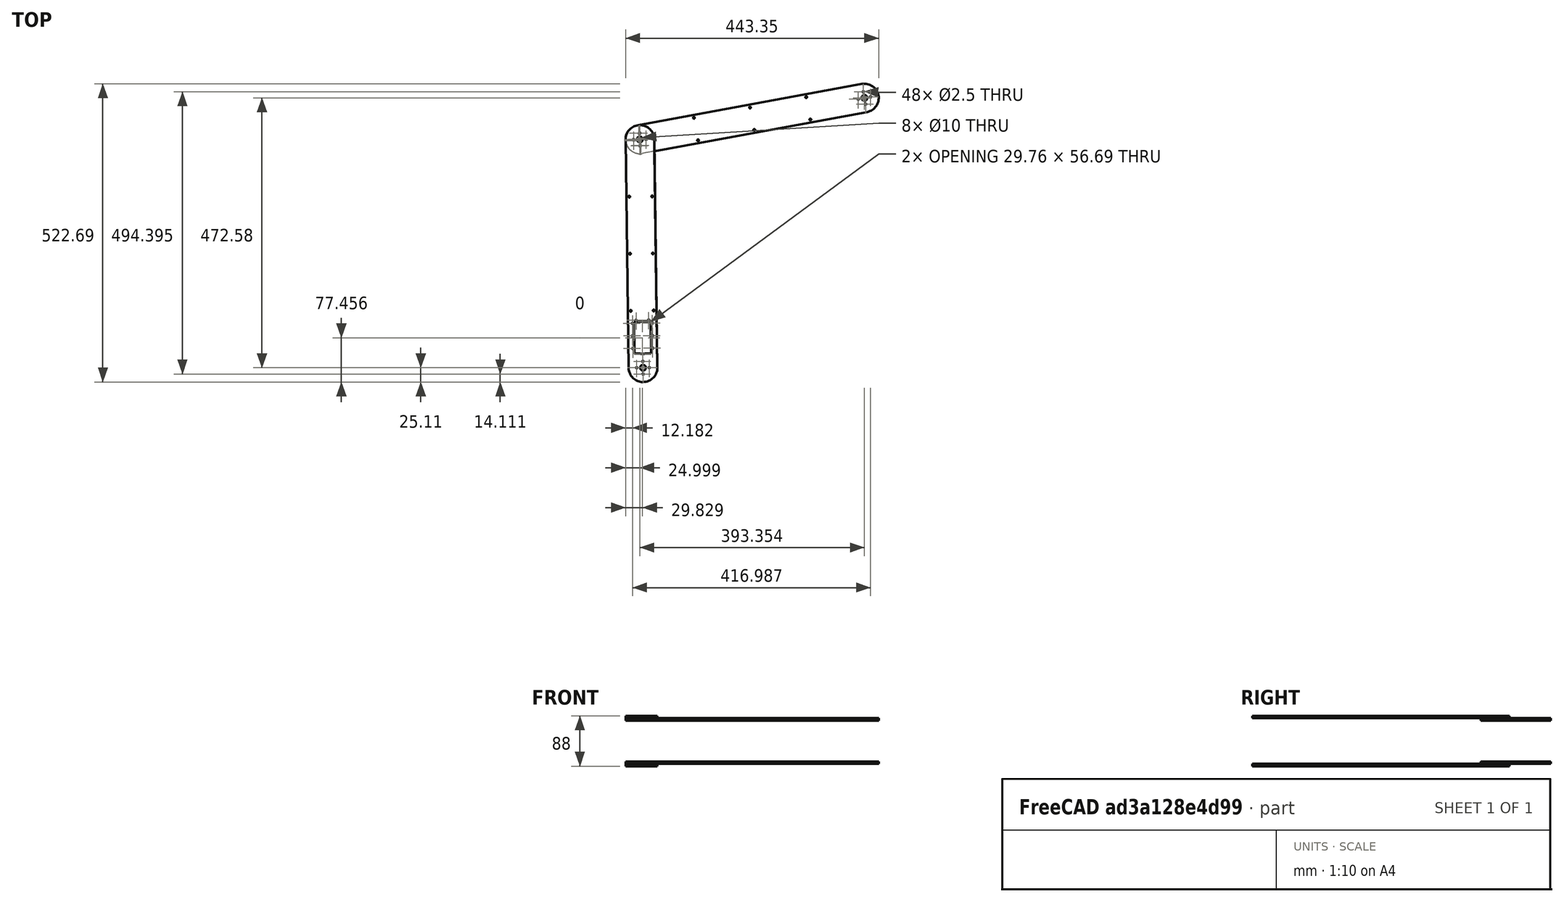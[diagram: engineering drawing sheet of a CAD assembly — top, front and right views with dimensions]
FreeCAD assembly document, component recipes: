
FREECAD ASSEMBLY — COMPONENT RECIPES ("arm_assembly4")

This assembly document has 12 components, labeled P0..P11 below (a component is one placed body or linked part). 8 of them carry a construction recipe — the FreeCAD feature program that regenerates the part from scratch, quoted from this document or its linked companion documents; the rest are supplied as boundary geometry only. No exploded tour is included for this assembly.
COMPONENT P0 — recipe-attached ("arm_low_1", modeled in this document).
Construction recipe (the document's own serialized feature program — sketch geometry with constraints, then the solid features built on it; lengths are millimeters unless a unit is written):

FEATURE [Sketcher::SketchObject] Sketch
  ArcFitTolerance = 1e-06
  AttachmentSupport = -> [XY_Plane]
  FullyConstrained = false
  MakeInternals = false
  MapMode = 5
  sketch-geometry (67):
    g0: LineSegment [constr] StartX=1.5008e-12 StartY=20 StartZ=0 EndX=1.5008e-12 EndY=-20 EndZ=0
    g1: LineSegment [constr] StartX=-2.359e-12 StartY=0 StartZ=0 EndX=-2.359e-12 EndY=400 EndZ=0
    g2: LineSegment [constr] StartX=1.5008e-12 StartY=20 StartZ=0 EndX=1.5008e-12 EndY=25 EndZ=0
    g3: Circle CenterX=-2.359e-12 CenterY=400 CenterZ=0 NormalX=0 NormalY=0 NormalZ=1 AngleXU=0 Radius=5
    g4: Circle CenterX=-2.359e-12 CenterY=400 CenterZ=0 NormalX=0 NormalY=0 NormalZ=1 AngleXU=0 Radius=2
    g5: Circle CenterX=-10.9997 CenterY=400 CenterZ=0 NormalX=0 NormalY=0 NormalZ=1 AngleXU=0 Radius=1.25
    g6: Circle CenterX=0 CenterY=389 CenterZ=0 NormalX=0 NormalY=0 NormalZ=1 AngleXU=0 Radius=1.25
    g7: Circle CenterX=10.9997 CenterY=400 CenterZ=0 NormalX=0 NormalY=0 NormalZ=1 AngleXU=0 Radius=1.25
    g8: Circle CenterX=0 CenterY=411 CenterZ=0 NormalX=0 NormalY=0 NormalZ=1 AngleXU=0 Radius=1.25
    g9: LineSegment [constr] StartX=0 StartY=-5 StartZ=0 EndX=0 EndY=5.99996 EndZ=0
    g10: Circle [constr] CenterX=0 CenterY=0 CenterZ=0 NormalX=0 NormalY=0 NormalZ=1 AngleXU=0 Radius=14
    g11: LineSegment [constr] StartX=0 StartY=0 StartZ=0 EndX=25.23 EndY=0 EndZ=0
    g12: Circle [constr] CenterX=0 CenterY=-3.8e-05 CenterZ=0 NormalX=0 NormalY=0 NormalZ=1 AngleXU=0 Radius=11
    g13: Circle CenterX=0 CenterY=0 CenterZ=0 NormalX=0 NormalY=0 NormalZ=1 AngleXU=0 Radius=5
    g14: Circle CenterX=10.9997 CenterY=0 CenterZ=0 NormalX=0 NormalY=0 NormalZ=1 AngleXU=0 Radius=1.25
    g15: Circle CenterX=-10.9997 CenterY=0 CenterZ=0 NormalX=0 NormalY=0 NormalZ=1 AngleXU=0 Radius=1.25
    g16: Circle CenterX=0 CenterY=-10.9997 CenterZ=0 NormalX=0 NormalY=0 NormalZ=1 AngleXU=0 Radius=1.25
    g17: Circle CenterX=0 CenterY=11 CenterZ=0 NormalX=0 NormalY=0 NormalZ=1 AngleXU=0 Radius=1.25
    g18: LineSegment [constr] StartX=0 StartY=0 StartZ=0 EndX=-25 EndY=0 EndZ=0
    g19: LineSegment [constr] StartX=20.1368 StartY=86.0999 StartZ=0 EndX=20.1368 EndY=24.9999 EndZ=0
    g20: LineSegment [constr] StartX=0.036848 StartY=80.5 StartZ=0 EndX=14.5368 EndY=80.5 EndZ=0
    g21: LineSegment StartX=14.5368 StartY=80.5 StartZ=0 EndX=-14.4632 EndY=80.5 EndZ=0
    g22: LineSegment StartX=14.5368 StartY=80.5 StartZ=0 EndX=14.5368 EndY=24.9999 EndZ=0
    g23: Circle CenterX=11.0368 CenterY=83.3 CenterZ=0 NormalX=0 NormalY=0 NormalZ=1 AngleXU=0 Radius=1.25
    g24: Circle CenterX=17.3368 CenterY=78 CenterZ=0 NormalX=0 NormalY=0 NormalZ=1 AngleXU=0 Radius=1.25
    g25: LineSegment [constr] StartX=-20.0632 StartY=86.0999 StartZ=0 EndX=20.1368 EndY=86.0999 EndZ=0
    g26: Circle CenterX=17.3368 CenterY=56 CenterZ=0 NormalX=0 NormalY=0 NormalZ=1 AngleXU=0 Radius=1.25
    g27: Circle CenterX=17.3368 CenterY=34 CenterZ=0 NormalX=0 NormalY=0 NormalZ=1 AngleXU=0 Radius=1.25
    g28: Circle [constr] CenterX=0.036848 CenterY=37.9999 CenterZ=0 NormalX=0 NormalY=0 NormalZ=1 AngleXU=0 Radius=14
    g29: ArcOfCircle CenterX=0.036848 CenterY=37.9999 CenterZ=0 NormalX=0 NormalY=0 NormalZ=1 AngleXU=0 Radius=14 StartAngle=4.33214 EndAngle=5.09264
    g30: LineSegment StartX=5.233 StartY=24.9999 StartZ=0 EndX=14.5368 EndY=24.9999 EndZ=0
    g31: LineSegment [constr] StartX=14.5368 StartY=24.9999 StartZ=0 EndX=20.1368 EndY=24.9999 EndZ=0
    g32: LineSegment [constr] StartX=17.3368 StartY=56 StartZ=0 EndX=-17.2632 EndY=56 EndZ=0
    g33: LineSegment [constr] StartX=-20.0632 StartY=24.9999 StartZ=0 EndX=-20.0632 EndY=86.0999 EndZ=0
    g34: LineSegment StartX=-14.4632 StartY=80.5 StartZ=0 EndX=-14.4632 EndY=24.9999 EndZ=0
    g35: Circle CenterX=-17.2632 CenterY=78 CenterZ=0 NormalX=0 NormalY=0 NormalZ=1 AngleXU=0 Radius=1.25
    g36: Circle CenterX=-10.9632 CenterY=83.3 CenterZ=0 NormalX=0 NormalY=0 NormalZ=1 AngleXU=0 Radius=1.25
    g37: Circle CenterX=-17.2632 CenterY=56 CenterZ=0 NormalX=0 NormalY=0 NormalZ=1 AngleXU=0 Radius=1.25
    g38: Circle CenterX=-17.2632 CenterY=34 CenterZ=0 NormalX=0 NormalY=0 NormalZ=1 AngleXU=0 Radius=1.25
    g39: LineSegment StartX=-14.4632 StartY=24.9999 StartZ=0 EndX=-5.15931 EndY=24.9999 EndZ=0
    g40: LineSegment [constr] StartX=-20.0632 StartY=24.9999 StartZ=0 EndX=-14.4632 EndY=24.9999 EndZ=0
    g41: ArcOfCircle CenterX=0.115002 CenterY=3.75548e-06 CenterZ=0 NormalX=0 NormalY=0 NormalZ=1 AngleXU=0 Radius=25.115 StartAngle=3.14159 EndAngle=6.28319
    g42: ArcOfCircle CenterX=0.115002 CenterY=399.959 CenterZ=0 NormalX=0 NormalY=0 NormalZ=1 AngleXU=0 Radius=25.115 StartAngle=0 EndAngle=3.14159
    g43: LineSegment StartX=-25 StartY=3.75548e-06 StartZ=0 EndX=-25 EndY=399.959 EndZ=0
    g44: LineSegment StartX=25.23 StartY=3.75548e-06 StartZ=0 EndX=25.23 EndY=399.959 EndZ=0
    g45: LineSegment [constr] StartX=25.23 StartY=199.98 StartZ=0 EndX=-25 EndY=199.98 EndZ=0
    g46: LineSegment [constr] StartX=25.23 StartY=199.98 StartZ=0 EndX=55.23 EndY=199.98 EndZ=0
    g47: LineSegment [constr] StartX=25.23 StartY=0 StartZ=0 EndX=55.23 EndY=0 EndZ=0
    g48: LineSegment [constr] StartX=55.23 StartY=0 StartZ=0 EndX=55.23 EndY=199.98 EndZ=0
    g49: LineSegment [constr] StartX=55.23 StartY=99.9898 StartZ=0 EndX=25.23 EndY=99.9898 EndZ=0
    g50: LineSegment [constr] StartX=25.23 StartY=99.9898 StartZ=0 EndX=-25 EndY=99.9898 EndZ=0
    g51: LineSegment [constr] StartX=25.23 StartY=399.959 StartZ=0 EndX=55.23 EndY=399.959 EndZ=0
    g52: LineSegment [constr] StartX=55.23 StartY=399.959 StartZ=0 EndX=55.23 EndY=199.98 EndZ=0
    g53: LineSegment [constr] StartX=55.23 StartY=299.969 StartZ=0 EndX=25.23 EndY=299.969 EndZ=0
    g54: LineSegment [constr] StartX=25.23 StartY=299.969 StartZ=0 EndX=-25 EndY=299.969 EndZ=0
    g55: LineSegment [constr] StartX=-25 StartY=299.969 StartZ=0 EndX=-20 EndY=299.969 EndZ=0
    g56: LineSegment [constr] StartX=-20 StartY=299.969 StartZ=0 EndX=-20 EndY=199.98 EndZ=0
    g57: LineSegment [constr] StartX=-20 StartY=199.98 StartZ=0 EndX=-20 EndY=99.9898 EndZ=0
    g58: LineSegment [constr] StartX=25.23 StartY=299.969 StartZ=0 EndX=20.23 EndY=299.969 EndZ=0
    g59: LineSegment [constr] StartX=20.23 StartY=299.969 StartZ=0 EndX=20.23 EndY=199.98 EndZ=0
    g60: LineSegment [constr] StartX=20.23 StartY=199.98 StartZ=0 EndX=20.23 EndY=99.9898 EndZ=0
    g61: Circle CenterX=-20 CenterY=299.969 CenterZ=0 NormalX=0 NormalY=0 NormalZ=1 AngleXU=0 Radius=1.5
    g62: Circle CenterX=20.23 CenterY=299.969 CenterZ=0 NormalX=0 NormalY=0 NormalZ=1 AngleXU=0 Radius=1.5
    g63: Circle CenterX=-20 CenterY=199.98 CenterZ=0 NormalX=0 NormalY=0 NormalZ=1 AngleXU=0 Radius=1.5
    g64: Circle CenterX=20.23 CenterY=199.98 CenterZ=0 NormalX=0 NormalY=0 NormalZ=1 AngleXU=0 Radius=1.5
    g65: Circle CenterX=-20 CenterY=99.9898 CenterZ=0 NormalX=0 NormalY=0 NormalZ=1 AngleXU=0 Radius=1.5
    g66: Circle CenterX=20.23 CenterY=99.9898 CenterZ=0 NormalX=0 NormalY=0 NormalZ=1 AngleXU=0 Radius=1.5
  constraints (132):
    c: Vertical(g0)
    c: Vertical(g1)
    c: Coincident(g2,g0)
    c: Vertical(g2)
    c: Diameter(g3) = 10
    c: Coincident(g3,g1)
    c: Diameter(g4) = 4
    c: Coincident(g4,g1)
    c: Diameter(g8) = 2.5
    c: Diameter(g5) = 2.5
    c: Diameter(g6) = 2.5
    c: Diameter(g7) = 2.5
    c: Vertical(g9)
    c: Diameter(g10) = 28
    c: Coincident(g18,g10)
    c: Horizontal(g18)
    c: Coincident(g11,g10)
    c: Horizontal(g11)
    c: Diameter(g12) = 22
    c: Diameter(g13) = 10
    c: Coincident(g13,g10)
    c: Diameter(g17) = 2.5
    c: Diameter(g15) = 2.5
    c: Diameter(g16) = 2.5
    c: Diameter(g14) = 2.5
    c: Coincident(g25,g19)
    c: Coincident(g33,g25)
    c: Horizontal(g25)
    c: Vertical(g19)
    c: Vertical(g33)
    c: Distance(g19,g33) = 40.2
    c: Distance(g25,g33) = 61.1
    c: Diameter(g29) = 28
    c: Horizontal(g20)
    c: Coincident(g21,g20)
    c: Horizontal(g21)
    c: Coincident(g34,g21)
    c: Vertical(g34)
    c: Coincident(g22,g20)
    c: Vertical(g22)
    c: Diameter(g23) = 2.5
    c: Equal(g23,g36)
    c: Equal(g23,g27)
    c: Equal(g23,g38)
    c: Equal(g23,g37)
    c: Equal(g23,g35)
    c: Equal(g23,g24)
    c: Equal(g23,g26)
    c: Coincident(g28,g29)
    c: PointOnObject(g29,g28)
    c: Coincident(g30,g29)
    c: Coincident(g30,g22)
    c: Horizontal(g30)
    c: Coincident(g31,g22)
    c: Coincident(g31,g19)
    c: Horizontal(g31)
    c: Coincident(g39,g34)
    c: Coincident(g39,g29)
    c: Horizontal(g39)
    c: Coincident(g40,g33)
    c: Coincident(g40,g34)
    c: Horizontal(g40)
    c: Coincident(g32,g26)
    c: Coincident(g32,g37)
    c: Horizontal(g32)
    c: DistanceY(g28,g1) = 362
    c: Tangent(g41,g43) = 1.5708
    c: Tangent(g41,g44) = -1.5708
    c: Tangent(g42,g43) = 1.5708
    c: Tangent(g42,g44) = -1.5708
    c: Equal(g41,g42)
    c: Symmetric(g44,g44,g45)
    c: Symmetric(g43,g43,g45)
    c: Horizontal(g45)
    c: Distance(g46) = 30
    c: Horizontal(g46)
    c: Coincident(g46,g45)
    c: Distance(g47) = 30
    c: Horizontal(g47)
    c: Coincident(g47,g11)
    c: PointOnObject(g47,g-1)
    c: Coincident(g48,g47)
    c: Coincident(g48,g46)
    c: Vertical(g48)
    c: Symmetric(g48,g48,g49)
    c: PointOnObject(g49,g44)
    c: Horizontal(g49)
    c: Coincident(g50,g49)
    c: PointOnObject(g50,g43)
    c: Horizontal(g50)
    c: Distance(g51) = 30
    c: Horizontal(g51)
    c: Coincident(g51,g42)
    c: Coincident(g52,g51)
    c: Coincident(g52,g46)
    c: Symmetric(g52,g52,g53)
    c: PointOnObject(g53,g44)
    c: Horizontal(g53)
    c: Coincident(g54,g53)
    c: PointOnObject(g54,g43)
    c: Horizontal(g54)
    c: Distance(g55) = 5
    c: Coincident(g55,g54)
    c: PointOnObject(g55,g54)
    c: Coincident(g56,g55)
    c: PointOnObject(g56,g45)
    c: Vertical(g56)
    c: Coincident(g57,g56)
    c: PointOnObject(g57,g50)
    c: Vertical(g57)
    c: Distance(g58) = 5
    c: Coincident(g58,g53)
    c: PointOnObject(g58,g54)
    c: Coincident(g59,g58)
    c: PointOnObject(g59,g45)
    c: Vertical(g59)
    c: Coincident(g60,g59)
    c: PointOnObject(g60,g50)
    c: Vertical(g60)
    c: Coincident(g61,g55)
    c: Diameter(g61) = 3
    c: Coincident(g62,g58)
    c: Equal(g61,g62)
    c: Coincident(g63,g56)
    c: Equal(g61,g63)
    c: Coincident(g64,g59)
    c: Equal(g63,g64)
    c: Coincident(g65,g57)
    c: Equal(g63,g65)
    c: Coincident(g66,g60)
    c: Equal(g65,g66)
    c: DistanceY(g41,g28) = 37.9999
FEATURE [PartDesign::Pad] Pad
  Direction = (0,0,1)
  Length = 4
  Length2 = 10
  Profile = -> Sketch
  ReferenceAxis = -> Sketch [N_Axis]
  Refine = true
  Suppressed = false
  Type = 0
FEATURE [PartDesign::Body] Body  label="arm_low_1"
  AllowCompound = false
  Group = -> [Sketch,Pad]
  Origin = -> Origin
  Placement = pos=(0,0,25.3) rot=(0,0,1;0.013804rad)
  Tip = -> Pad
COMPONENT P1 — recipe-attached ("arm_high_1", modeled in this document).
Construction recipe (the document's own serialized feature program — sketch geometry with constraints, then the solid features built on it; lengths are millimeters unless a unit is written):

FEATURE [Sketcher::SketchObject] Sketch001
  ArcFitTolerance = 1e-06
  FullyConstrained = false
  MakeInternals = false
  MapMode = 5
  sketch-geometry (41):
    g0: Circle [constr] CenterX=7e-16 CenterY=0.000303 CenterZ=0 NormalX=0 NormalY=0 NormalZ=1 AngleXU=0 Radius=14
    g1: LineSegment [constr] StartX=7e-16 StartY=0.000303 StartZ=0 EndX=7e-16 EndY=400.001 EndZ=0
    g2: Circle CenterX=7e-16 CenterY=400.001 CenterZ=0 NormalX=0 NormalY=0 NormalZ=1 AngleXU=0 Radius=5
    g3: Circle CenterX=7e-16 CenterY=0 CenterZ=0 NormalX=0 NormalY=0 NormalZ=1 AngleXU=0 Radius=5
    g4: Circle CenterX=7e-16 CenterY=400.001 CenterZ=0 NormalX=0 NormalY=0 NormalZ=1 AngleXU=0 Radius=2
    g5: Circle CenterX=7e-16 CenterY=0.000303 CenterZ=0 NormalX=0 NormalY=0 NormalZ=1 AngleXU=0 Radius=2
    g6: Circle [constr] CenterX=0 CenterY=0 CenterZ=0 NormalX=0 NormalY=0 NormalZ=1 AngleXU=0 Radius=11
    g7: ArcOfCircle CenterX=7e-16 CenterY=0 CenterZ=0 NormalX=0 NormalY=0 NormalZ=1 AngleXU=0 Radius=25 StartAngle=3.14159 EndAngle=6.28319
    g8: ArcOfCircle CenterX=7e-16 CenterY=400.001 CenterZ=0 NormalX=0 NormalY=0 NormalZ=1 AngleXU=0 Radius=25 StartAngle=6e-16 EndAngle=3.14159
    g9: LineSegment StartX=-25 StartY=-8e-15 StartZ=0 EndX=-25 EndY=400.001 EndZ=0
    g10: LineSegment StartX=25 StartY=0 StartZ=0 EndX=25 EndY=400.001 EndZ=0
    g11: Circle CenterX=10.9997 CenterY=400.001 CenterZ=0 NormalX=0 NormalY=0 NormalZ=1 AngleXU=0 Radius=1.25
    g12: Circle CenterX=0 CenterY=411.001 CenterZ=0 NormalX=0 NormalY=0 NormalZ=1 AngleXU=0 Radius=1.25
    g13: Circle CenterX=-10.9997 CenterY=400.001 CenterZ=0 NormalX=0 NormalY=0 NormalZ=1 AngleXU=0 Radius=1.25
    g14: Circle CenterX=0 CenterY=389.001 CenterZ=0 NormalX=0 NormalY=0 NormalZ=1 AngleXU=0 Radius=1.25
    g15: Circle CenterX=10.9997 CenterY=0.000303 CenterZ=0 NormalX=0 NormalY=0 NormalZ=1 AngleXU=0 Radius=1.25
    g16: Circle CenterX=0 CenterY=11 CenterZ=0 NormalX=0 NormalY=0 NormalZ=1 AngleXU=0 Radius=1.25
    g17: Circle CenterX=-10.9997 CenterY=0.000303 CenterZ=0 NormalX=0 NormalY=0 NormalZ=1 AngleXU=0 Radius=1.25
    g18: Circle CenterX=0 CenterY=-10.9994 CenterZ=0 NormalX=0 NormalY=0 NormalZ=1 AngleXU=0 Radius=1.25
    g19: LineSegment [constr] StartX=25 StartY=200 StartZ=0 EndX=-25 EndY=200 EndZ=0
    g20: LineSegment [constr] StartX=25 StartY=200 StartZ=0 EndX=55 EndY=200 EndZ=0
    g21: LineSegment [constr] StartX=25 StartY=0 StartZ=0 EndX=55 EndY=0 EndZ=0
    g22: LineSegment [constr] StartX=25 StartY=400.001 StartZ=0 EndX=55 EndY=400.001 EndZ=0
    g23: LineSegment [constr] StartX=55 StartY=200 StartZ=0 EndX=55 EndY=400.001 EndZ=0
    g24: LineSegment [constr] StartX=55 StartY=200 StartZ=0 EndX=55 EndY=0 EndZ=0
    g25: LineSegment [constr] StartX=55 StartY=100 StartZ=0 EndX=25 EndY=100 EndZ=0
    g26: LineSegment [constr] StartX=25 StartY=100 StartZ=0 EndX=-25 EndY=100 EndZ=0
    g27: LineSegment [constr] StartX=55 StartY=300 StartZ=0 EndX=25 EndY=300 EndZ=0
    g28: LineSegment [constr] StartX=25 StartY=300 StartZ=0 EndX=-25 EndY=300 EndZ=0
    g29: LineSegment [constr] StartX=-25 StartY=300 StartZ=0 EndX=-20 EndY=300 EndZ=0
    g30: LineSegment [constr] StartX=-20 StartY=300 StartZ=0 EndX=-20 EndY=200 EndZ=0
    g31: LineSegment [constr] StartX=-20 StartY=200 StartZ=0 EndX=-20 EndY=100 EndZ=0
    g32: LineSegment [constr] StartX=25 StartY=100 StartZ=0 EndX=20 EndY=100 EndZ=0
    g33: LineSegment [constr] StartX=20 StartY=100 StartZ=0 EndX=20 EndY=200 EndZ=0
    g34: LineSegment [constr] StartX=20 StartY=200 StartZ=0 EndX=20 EndY=300 EndZ=0
    g35: Circle CenterX=-20 CenterY=300 CenterZ=0 NormalX=0 NormalY=0 NormalZ=1 AngleXU=0 Radius=1.5
    g36: Circle CenterX=20 CenterY=300 CenterZ=0 NormalX=0 NormalY=0 NormalZ=1 AngleXU=0 Radius=1.5
    g37: Circle CenterX=-20 CenterY=200 CenterZ=0 NormalX=0 NormalY=0 NormalZ=1 AngleXU=0 Radius=1.5
    g38: Circle CenterX=20 CenterY=200 CenterZ=0 NormalX=0 NormalY=0 NormalZ=1 AngleXU=0 Radius=1.5
    g39: Circle CenterX=-20 CenterY=100 CenterZ=0 NormalX=0 NormalY=0 NormalZ=1 AngleXU=0 Radius=1.5
    g40: Circle CenterX=20 CenterY=100 CenterZ=0 NormalX=0 NormalY=0 NormalZ=1 AngleXU=0 Radius=1.5
  constraints (85):
    c: Diameter(g0) = 28
    c: Coincident(g1,g0)
    c: Vertical(g1)
    c: Coincident(g2,g1)
    c: Diameter(g3) = 10
    c: Diameter(g4) = 4
    c: Coincident(g4,g1)
    c: Diameter(g5) = 4
    c: Coincident(g5,g0)
    c: Diameter(g6) = 22
    c: Tangent(g7,g9) = 1.5708
    c: Tangent(g7,g10) = -1.5708
    c: Tangent(g8,g9) = 1.5708
    c: Tangent(g8,g10) = -1.5708
    c: Equal(g7,g8)
    c: Radius(g7) = 25
    c: Coincident(g7,g3)
    c: Coincident(g8,g1)
    c: Vertical(g9)
    c: Diameter(g12) = 2.5
    c: Diameter(g13) = 2.5
    c: Diameter(g14) = 2.5
    c: Diameter(g11) = 2.5
    c: Diameter(g16) = 2.5
    c: Diameter(g17) = 2.5
    c: Diameter(g18) = 2.5
    c: Diameter(g15) = 2.5
    c: Symmetric(g10,g10,g19)
    c: Symmetric(g9,g9,g19)
    c: Distance(g20) = 30
    c: Horizontal(g20)
    c: Coincident(g20,g19)
    c: Distance(g21) = 30
    c: Horizontal(g21)
    c: Coincident(g21,g7)
    c: PointOnObject(g21,g-1)
    c: Distance(g22) = 30
    c: Horizontal(g22)
    c: Coincident(g22,g8)
    c: Coincident(g23,g20)
    c: Coincident(g23,g22)
    c: Coincident(g24,g20)
    c: Coincident(g24,g21)
    c: Symmetric(g24,g24,g25)
    c: PointOnObject(g25,g10)
    c: Horizontal(g25)
    c: Coincident(g26,g25)
    c: PointOnObject(g26,g9)
    c: Horizontal(g26)
    c: Symmetric(g23,g23,g27)
    c: PointOnObject(g27,g10)
    c: Horizontal(g27)
    c: Coincident(g28,g27)
    c: PointOnObject(g28,g9)
    c: Horizontal(g28)
    c: Distance(g29) = 5
    c: Horizontal(g29)
    c: Coincident(g29,g28)
    c: Coincident(g30,g29)
    c: PointOnObject(g30,g19)
    c: Vertical(g30)
    c: Coincident(g31,g30)
    c: PointOnObject(g31,g26)
    c: Vertical(g31)
    c: Distance(g32) = 5
    c: Horizontal(g32)
    c: Coincident(g32,g25)
    c: Coincident(g33,g32)
    c: PointOnObject(g33,g19)
    c: Vertical(g33)
    c: Coincident(g34,g33)
    c: PointOnObject(g34,g28)
    c: Vertical(g34)
    c: Diameter(g35) = 3
    c: Coincident(g35,g29)
    c: Coincident(g36,g34)
    c: Equal(g35,g36)
    c: Coincident(g37,g30)
    c: Equal(g35,g37)
    c: Coincident(g38,g33)
    c: Equal(g37,g38)
    c: Coincident(g39,g31)
    c: Equal(g37,g39)
    c: Coincident(g40,g32)
    c: Equal(g39,g40)
FEATURE [PartDesign::Pad] Pad001
  Direction = (0,0,1)
  Length = 4
  Length2 = 10
  Profile = -> Sketch001
  ReferenceAxis = -> Sketch001 [N_Axis]
  Refine = true
  Suppressed = false
  Type = 0
FEATURE [PartDesign::Body] Body001  label="arm_high_1"
  AllowCompound = false
  Group = -> [Sketch001,Pad001]
  Origin = -> Origin001
  Placement = pos=(387.832,472.58,29.3) rot=(0,0,1;1.75335rad)
  Tip = -> Pad001
COMPONENT P2 — same part as P0; its construction recipe is shown at P0.
COMPONENT P3 — same part as P0; its construction recipe is shown at P0.
COMPONENT P4 — recipe-attached ("arm_low_002", modeled in this document).
Construction recipe (the document's own serialized feature program — sketch geometry with constraints, then the solid features built on it; lengths are millimeters unless a unit is written):

FEATURE [Sketcher::SketchObject] Sketch002
  ArcFitTolerance = 1e-06
  AttachmentSupport = -> [XY_Plane004]
  FullyConstrained = false
  MakeInternals = false
  MapMode = 5
  sketch-geometry (67):
    g0: LineSegment [constr] StartX=1.5008e-12 StartY=20 StartZ=0 EndX=1.5008e-12 EndY=-20 EndZ=0
    g1: LineSegment [constr] StartX=-2.359e-12 StartY=0 StartZ=0 EndX=-2.359e-12 EndY=400 EndZ=0
    g2: LineSegment [constr] StartX=1.5008e-12 StartY=20 StartZ=0 EndX=1.5008e-12 EndY=25 EndZ=0
    g3: Circle CenterX=-2.359e-12 CenterY=400 CenterZ=0 NormalX=0 NormalY=0 NormalZ=1 AngleXU=0 Radius=5
    g4: Circle CenterX=-2.359e-12 CenterY=400 CenterZ=0 NormalX=0 NormalY=0 NormalZ=1 AngleXU=0 Radius=2
    g5: Circle CenterX=-10.9997 CenterY=400 CenterZ=0 NormalX=0 NormalY=0 NormalZ=1 AngleXU=0 Radius=1.25
    g6: Circle CenterX=0 CenterY=389 CenterZ=0 NormalX=0 NormalY=0 NormalZ=1 AngleXU=0 Radius=1.25
    g7: Circle CenterX=10.9997 CenterY=400 CenterZ=0 NormalX=0 NormalY=0 NormalZ=1 AngleXU=0 Radius=1.25
    g8: Circle CenterX=0 CenterY=411 CenterZ=0 NormalX=0 NormalY=0 NormalZ=1 AngleXU=0 Radius=1.25
    g9: LineSegment [constr] StartX=0 StartY=-5 StartZ=0 EndX=0 EndY=5.99996 EndZ=0
    g10: Circle [constr] CenterX=0 CenterY=0 CenterZ=0 NormalX=0 NormalY=0 NormalZ=1 AngleXU=0 Radius=14
    g11: LineSegment [constr] StartX=0 StartY=0 StartZ=0 EndX=25.23 EndY=0 EndZ=0
    g12: Circle [constr] CenterX=0 CenterY=-3.8e-05 CenterZ=0 NormalX=0 NormalY=0 NormalZ=1 AngleXU=0 Radius=11
    g13: Circle CenterX=0 CenterY=0 CenterZ=0 NormalX=0 NormalY=0 NormalZ=1 AngleXU=0 Radius=5
    g14: Circle CenterX=10.9997 CenterY=0 CenterZ=0 NormalX=0 NormalY=0 NormalZ=1 AngleXU=0 Radius=1.25
    g15: Circle CenterX=-10.9997 CenterY=0 CenterZ=0 NormalX=0 NormalY=0 NormalZ=1 AngleXU=0 Radius=1.25
    g16: Circle CenterX=0 CenterY=-10.9997 CenterZ=0 NormalX=0 NormalY=0 NormalZ=1 AngleXU=0 Radius=1.25
    g17: Circle CenterX=0 CenterY=11 CenterZ=0 NormalX=0 NormalY=0 NormalZ=1 AngleXU=0 Radius=1.25
    g18: LineSegment [constr] StartX=0 StartY=0 StartZ=0 EndX=-25 EndY=0 EndZ=0
    g19: LineSegment [constr] StartX=20.1368 StartY=86.0999 StartZ=0 EndX=20.1368 EndY=24.9999 EndZ=0
    g20: LineSegment [constr] StartX=0.036848 StartY=80.5 StartZ=0 EndX=14.5368 EndY=80.5 EndZ=0
    g21: LineSegment StartX=14.5368 StartY=80.5 StartZ=0 EndX=-14.4632 EndY=80.5 EndZ=0
    g22: LineSegment StartX=14.5368 StartY=80.5 StartZ=0 EndX=14.5368 EndY=24.9999 EndZ=0
    g23: Circle CenterX=11.0368 CenterY=83.3 CenterZ=0 NormalX=0 NormalY=0 NormalZ=1 AngleXU=0 Radius=1.25
    g24: Circle CenterX=17.3368 CenterY=78 CenterZ=0 NormalX=0 NormalY=0 NormalZ=1 AngleXU=0 Radius=1.25
    g25: LineSegment [constr] StartX=-20.0632 StartY=86.0999 StartZ=0 EndX=20.1368 EndY=86.0999 EndZ=0
    g26: Circle CenterX=17.3368 CenterY=56 CenterZ=0 NormalX=0 NormalY=0 NormalZ=1 AngleXU=0 Radius=1.25
    g27: Circle CenterX=17.3368 CenterY=34 CenterZ=0 NormalX=0 NormalY=0 NormalZ=1 AngleXU=0 Radius=1.25
    g28: Circle [constr] CenterX=0.036848 CenterY=37.9999 CenterZ=0 NormalX=0 NormalY=0 NormalZ=1 AngleXU=0 Radius=14
    g29: ArcOfCircle CenterX=0.036848 CenterY=37.9999 CenterZ=0 NormalX=0 NormalY=0 NormalZ=1 AngleXU=0 Radius=14 StartAngle=4.33214 EndAngle=5.09264
    g30: LineSegment StartX=5.233 StartY=24.9999 StartZ=0 EndX=14.5368 EndY=24.9999 EndZ=0
    g31: LineSegment [constr] StartX=14.5368 StartY=24.9999 StartZ=0 EndX=20.1368 EndY=24.9999 EndZ=0
    g32: LineSegment [constr] StartX=17.3368 StartY=56 StartZ=0 EndX=-17.2632 EndY=56 EndZ=0
    g33: LineSegment [constr] StartX=-20.0632 StartY=24.9999 StartZ=0 EndX=-20.0632 EndY=86.0999 EndZ=0
    g34: LineSegment StartX=-14.4632 StartY=80.5 StartZ=0 EndX=-14.4632 EndY=24.9999 EndZ=0
    g35: Circle CenterX=-17.2632 CenterY=78 CenterZ=0 NormalX=0 NormalY=0 NormalZ=1 AngleXU=0 Radius=1.25
    g36: Circle CenterX=-10.9632 CenterY=83.3 CenterZ=0 NormalX=0 NormalY=0 NormalZ=1 AngleXU=0 Radius=1.25
    g37: Circle CenterX=-17.2632 CenterY=56 CenterZ=0 NormalX=0 NormalY=0 NormalZ=1 AngleXU=0 Radius=1.25
    g38: Circle CenterX=-17.2632 CenterY=34 CenterZ=0 NormalX=0 NormalY=0 NormalZ=1 AngleXU=0 Radius=1.25
    g39: LineSegment StartX=-14.4632 StartY=24.9999 StartZ=0 EndX=-5.15931 EndY=24.9999 EndZ=0
    g40: LineSegment [constr] StartX=-20.0632 StartY=24.9999 StartZ=0 EndX=-14.4632 EndY=24.9999 EndZ=0
    g41: ArcOfCircle CenterX=0.115002 CenterY=3.75548e-06 CenterZ=0 NormalX=0 NormalY=0 NormalZ=1 AngleXU=0 Radius=25.115 StartAngle=3.14159 EndAngle=6.28319
    g42: ArcOfCircle CenterX=0.115002 CenterY=399.959 CenterZ=0 NormalX=0 NormalY=0 NormalZ=1 AngleXU=0 Radius=25.115 StartAngle=0 EndAngle=3.14159
    g43: LineSegment StartX=-25 StartY=3.75548e-06 StartZ=0 EndX=-25 EndY=399.959 EndZ=0
    g44: LineSegment StartX=25.23 StartY=3.75548e-06 StartZ=0 EndX=25.23 EndY=399.959 EndZ=0
    g45: LineSegment [constr] StartX=25.23 StartY=199.98 StartZ=0 EndX=-25 EndY=199.98 EndZ=0
    g46: LineSegment [constr] StartX=25.23 StartY=199.98 StartZ=0 EndX=55.23 EndY=199.98 EndZ=0
    g47: LineSegment [constr] StartX=25.23 StartY=0 StartZ=0 EndX=55.23 EndY=0 EndZ=0
    g48: LineSegment [constr] StartX=55.23 StartY=0 StartZ=0 EndX=55.23 EndY=199.98 EndZ=0
    g49: LineSegment [constr] StartX=55.23 StartY=99.9898 StartZ=0 EndX=25.23 EndY=99.9898 EndZ=0
    g50: LineSegment [constr] StartX=25.23 StartY=99.9898 StartZ=0 EndX=-25 EndY=99.9898 EndZ=0
    g51: LineSegment [constr] StartX=25.23 StartY=399.959 StartZ=0 EndX=55.23 EndY=399.959 EndZ=0
    g52: LineSegment [constr] StartX=55.23 StartY=399.959 StartZ=0 EndX=55.23 EndY=199.98 EndZ=0
    g53: LineSegment [constr] StartX=55.23 StartY=299.969 StartZ=0 EndX=25.23 EndY=299.969 EndZ=0
    g54: LineSegment [constr] StartX=25.23 StartY=299.969 StartZ=0 EndX=-25 EndY=299.969 EndZ=0
    g55: LineSegment [constr] StartX=-25 StartY=299.969 StartZ=0 EndX=-20 EndY=299.969 EndZ=0
    g56: LineSegment [constr] StartX=-20 StartY=299.969 StartZ=0 EndX=-20 EndY=199.98 EndZ=0
    g57: LineSegment [constr] StartX=-20 StartY=199.98 StartZ=0 EndX=-20 EndY=99.9898 EndZ=0
    g58: LineSegment [constr] StartX=25.23 StartY=299.969 StartZ=0 EndX=20.23 EndY=299.969 EndZ=0
    g59: LineSegment [constr] StartX=20.23 StartY=299.969 StartZ=0 EndX=20.23 EndY=199.98 EndZ=0
    g60: LineSegment [constr] StartX=20.23 StartY=199.98 StartZ=0 EndX=20.23 EndY=99.9898 EndZ=0
    g61: Circle CenterX=-20 CenterY=299.969 CenterZ=0 NormalX=0 NormalY=0 NormalZ=1 AngleXU=0 Radius=1.5
    g62: Circle CenterX=20.23 CenterY=299.969 CenterZ=0 NormalX=0 NormalY=0 NormalZ=1 AngleXU=0 Radius=1.5
    g63: Circle CenterX=-20 CenterY=199.98 CenterZ=0 NormalX=0 NormalY=0 NormalZ=1 AngleXU=0 Radius=1.5
    g64: Circle CenterX=20.23 CenterY=199.98 CenterZ=0 NormalX=0 NormalY=0 NormalZ=1 AngleXU=0 Radius=1.5
    g65: Circle CenterX=-20 CenterY=99.9898 CenterZ=0 NormalX=0 NormalY=0 NormalZ=1 AngleXU=0 Radius=1.5
    g66: Circle CenterX=20.23 CenterY=99.9898 CenterZ=0 NormalX=0 NormalY=0 NormalZ=1 AngleXU=0 Radius=1.5
  constraints (132):
    c: Vertical(g0)
    c: Vertical(g1)
    c: Coincident(g2,g0)
    c: Vertical(g2)
    c: Diameter(g3) = 10
    c: Coincident(g3,g1)
    c: Diameter(g4) = 4
    c: Coincident(g4,g1)
    c: Diameter(g8) = 2.5
    c: Diameter(g5) = 2.5
    c: Diameter(g6) = 2.5
    c: Diameter(g7) = 2.5
    c: Vertical(g9)
    c: Diameter(g10) = 28
    c: Coincident(g18,g10)
    c: Horizontal(g18)
    c: Coincident(g11,g10)
    c: Horizontal(g11)
    c: Diameter(g12) = 22
    c: Diameter(g13) = 10
    c: Coincident(g13,g10)
    c: Diameter(g17) = 2.5
    c: Diameter(g15) = 2.5
    c: Diameter(g16) = 2.5
    c: Diameter(g14) = 2.5
    c: Coincident(g25,g19)
    c: Coincident(g33,g25)
    c: Horizontal(g25)
    c: Vertical(g19)
    c: Vertical(g33)
    c: Distance(g19,g33) = 40.2
    c: Distance(g25,g33) = 61.1
    c: Diameter(g29) = 28
    c: Horizontal(g20)
    c: Coincident(g21,g20)
    c: Horizontal(g21)
    c: Coincident(g34,g21)
    c: Vertical(g34)
    c: Coincident(g22,g20)
    c: Vertical(g22)
    c: Diameter(g23) = 2.5
    c: Equal(g23,g36)
    c: Equal(g23,g27)
    c: Equal(g23,g38)
    c: Equal(g23,g37)
    c: Equal(g23,g35)
    c: Equal(g23,g24)
    c: Equal(g23,g26)
    c: Coincident(g28,g29)
    c: PointOnObject(g29,g28)
    c: Coincident(g30,g29)
    c: Coincident(g30,g22)
    c: Horizontal(g30)
    c: Coincident(g31,g22)
    c: Coincident(g31,g19)
    c: Horizontal(g31)
    c: Coincident(g39,g34)
    c: Coincident(g39,g29)
    c: Horizontal(g39)
    c: Coincident(g40,g33)
    c: Coincident(g40,g34)
    c: Horizontal(g40)
    c: Coincident(g32,g26)
    c: Coincident(g32,g37)
    c: Horizontal(g32)
    c: DistanceY(g28,g1) = 362
    c: Tangent(g41,g43) = 1.5708
    c: Tangent(g41,g44) = -1.5708
    c: Tangent(g42,g43) = 1.5708
    c: Tangent(g42,g44) = -1.5708
    c: Equal(g41,g42)
    c: Symmetric(g44,g44,g45)
    c: Symmetric(g43,g43,g45)
    c: Horizontal(g45)
    c: Distance(g46) = 30
    c: Horizontal(g46)
    c: Coincident(g46,g45)
    c: Distance(g47) = 30
    c: Horizontal(g47)
    c: Coincident(g47,g11)
    c: PointOnObject(g47,g-1)
    c: Coincident(g48,g47)
    c: Coincident(g48,g46)
    c: Vertical(g48)
    c: Symmetric(g48,g48,g49)
    c: PointOnObject(g49,g44)
    c: Horizontal(g49)
    c: Coincident(g50,g49)
    c: PointOnObject(g50,g43)
    c: Horizontal(g50)
    c: Distance(g51) = 30
    c: Horizontal(g51)
    c: Coincident(g51,g42)
    c: Coincident(g52,g51)
    c: Coincident(g52,g46)
    c: Symmetric(g52,g52,g53)
    c: PointOnObject(g53,g44)
    c: Horizontal(g53)
    c: Coincident(g54,g53)
    c: PointOnObject(g54,g43)
    c: Horizontal(g54)
    c: Distance(g55) = 5
    c: Coincident(g55,g54)
    c: PointOnObject(g55,g54)
    c: Coincident(g56,g55)
    c: PointOnObject(g56,g45)
    c: Vertical(g56)
    c: Coincident(g57,g56)
    c: PointOnObject(g57,g50)
    c: Vertical(g57)
    c: Distance(g58) = 5
    c: Coincident(g58,g53)
    c: PointOnObject(g58,g54)
    c: Coincident(g59,g58)
    c: PointOnObject(g59,g45)
    c: Vertical(g59)
    c: Coincident(g60,g59)
    c: PointOnObject(g60,g50)
    c: Vertical(g60)
    c: Coincident(g61,g55)
    c: Diameter(g61) = 3
    c: Coincident(g62,g58)
    c: Equal(g61,g62)
    c: Coincident(g63,g56)
    c: Equal(g61,g63)
    c: Coincident(g64,g59)
    c: Equal(g63,g64)
    c: Coincident(g65,g57)
    c: Equal(g63,g65)
    c: Coincident(g66,g60)
    c: Equal(g65,g66)
    c: DistanceY(g41,g28) = 37.9999
FEATURE [PartDesign::Pad] Pad002
  Direction = (0,0,1)
  Length = 4
  Length2 = 10
  Profile = -> Sketch002
  ReferenceAxis = -> Sketch002 [N_Axis]
  Refine = true
  Suppressed = false
  Type = 0
FEATURE [PartDesign::Body] Body004  label="arm_low_002"
  AllowCompound = false
  Group = -> [Sketch002,Pad002]
  Origin = -> Origin004
  Placement = pos=(0,0,109.3) rot=(0,0,1;0.013804rad)
  Tip = -> Pad002
COMPONENT P5 — recipe-attached ("arm_high_002", modeled in this document).
Construction recipe (the document's own serialized feature program — sketch geometry with constraints, then the solid features built on it; lengths are millimeters unless a unit is written):

FEATURE [Sketcher::SketchObject] Sketch003
  ArcFitTolerance = 1e-06
  FullyConstrained = false
  MakeInternals = false
  MapMode = 5
  sketch-geometry (41):
    g0: Circle [constr] CenterX=7e-16 CenterY=0.000303 CenterZ=0 NormalX=0 NormalY=0 NormalZ=1 AngleXU=0 Radius=14
    g1: LineSegment [constr] StartX=7e-16 StartY=0.000303 StartZ=0 EndX=7e-16 EndY=400.001 EndZ=0
    g2: Circle CenterX=7e-16 CenterY=400.001 CenterZ=0 NormalX=0 NormalY=0 NormalZ=1 AngleXU=0 Radius=5
    g3: Circle CenterX=7e-16 CenterY=0 CenterZ=0 NormalX=0 NormalY=0 NormalZ=1 AngleXU=0 Radius=5
    g4: Circle CenterX=7e-16 CenterY=400.001 CenterZ=0 NormalX=0 NormalY=0 NormalZ=1 AngleXU=0 Radius=2
    g5: Circle CenterX=7e-16 CenterY=0.000303 CenterZ=0 NormalX=0 NormalY=0 NormalZ=1 AngleXU=0 Radius=2
    g6: Circle [constr] CenterX=0 CenterY=0 CenterZ=0 NormalX=0 NormalY=0 NormalZ=1 AngleXU=0 Radius=11
    g7: ArcOfCircle CenterX=7e-16 CenterY=0 CenterZ=0 NormalX=0 NormalY=0 NormalZ=1 AngleXU=0 Radius=25 StartAngle=3.14159 EndAngle=6.28319
    g8: ArcOfCircle CenterX=7e-16 CenterY=400.001 CenterZ=0 NormalX=0 NormalY=0 NormalZ=1 AngleXU=0 Radius=25 StartAngle=6e-16 EndAngle=3.14159
    g9: LineSegment StartX=-25 StartY=-8e-15 StartZ=0 EndX=-25 EndY=400.001 EndZ=0
    g10: LineSegment StartX=25 StartY=0 StartZ=0 EndX=25 EndY=400.001 EndZ=0
    g11: Circle CenterX=10.9997 CenterY=400.001 CenterZ=0 NormalX=0 NormalY=0 NormalZ=1 AngleXU=0 Radius=1.25
    g12: Circle CenterX=0 CenterY=411.001 CenterZ=0 NormalX=0 NormalY=0 NormalZ=1 AngleXU=0 Radius=1.25
    g13: Circle CenterX=-10.9997 CenterY=400.001 CenterZ=0 NormalX=0 NormalY=0 NormalZ=1 AngleXU=0 Radius=1.25
    g14: Circle CenterX=0 CenterY=389.001 CenterZ=0 NormalX=0 NormalY=0 NormalZ=1 AngleXU=0 Radius=1.25
    g15: Circle CenterX=10.9997 CenterY=0.000303 CenterZ=0 NormalX=0 NormalY=0 NormalZ=1 AngleXU=0 Radius=1.25
    g16: Circle CenterX=0 CenterY=11 CenterZ=0 NormalX=0 NormalY=0 NormalZ=1 AngleXU=0 Radius=1.25
    g17: Circle CenterX=-10.9997 CenterY=0.000303 CenterZ=0 NormalX=0 NormalY=0 NormalZ=1 AngleXU=0 Radius=1.25
    g18: Circle CenterX=0 CenterY=-10.9994 CenterZ=0 NormalX=0 NormalY=0 NormalZ=1 AngleXU=0 Radius=1.25
    g19: LineSegment [constr] StartX=25 StartY=200 StartZ=0 EndX=-25 EndY=200 EndZ=0
    g20: LineSegment [constr] StartX=25 StartY=200 StartZ=0 EndX=55 EndY=200 EndZ=0
    g21: LineSegment [constr] StartX=25 StartY=0 StartZ=0 EndX=55 EndY=0 EndZ=0
    g22: LineSegment [constr] StartX=25 StartY=400.001 StartZ=0 EndX=55 EndY=400.001 EndZ=0
    g23: LineSegment [constr] StartX=55 StartY=200 StartZ=0 EndX=55 EndY=400.001 EndZ=0
    g24: LineSegment [constr] StartX=55 StartY=200 StartZ=0 EndX=55 EndY=0 EndZ=0
    g25: LineSegment [constr] StartX=55 StartY=100 StartZ=0 EndX=25 EndY=100 EndZ=0
    g26: LineSegment [constr] StartX=25 StartY=100 StartZ=0 EndX=-25 EndY=100 EndZ=0
    g27: LineSegment [constr] StartX=55 StartY=300 StartZ=0 EndX=25 EndY=300 EndZ=0
    g28: LineSegment [constr] StartX=25 StartY=300 StartZ=0 EndX=-25 EndY=300 EndZ=0
    g29: LineSegment [constr] StartX=-25 StartY=300 StartZ=0 EndX=-20 EndY=300 EndZ=0
    g30: LineSegment [constr] StartX=-20 StartY=300 StartZ=0 EndX=-20 EndY=200 EndZ=0
    g31: LineSegment [constr] StartX=-20 StartY=200 StartZ=0 EndX=-20 EndY=100 EndZ=0
    g32: LineSegment [constr] StartX=25 StartY=100 StartZ=0 EndX=20 EndY=100 EndZ=0
    g33: LineSegment [constr] StartX=20 StartY=100 StartZ=0 EndX=20 EndY=200 EndZ=0
    g34: LineSegment [constr] StartX=20 StartY=200 StartZ=0 EndX=20 EndY=300 EndZ=0
    g35: Circle CenterX=-20 CenterY=300 CenterZ=0 NormalX=0 NormalY=0 NormalZ=1 AngleXU=0 Radius=1.5
    g36: Circle CenterX=20 CenterY=300 CenterZ=0 NormalX=0 NormalY=0 NormalZ=1 AngleXU=0 Radius=1.5
    g37: Circle CenterX=-20 CenterY=200 CenterZ=0 NormalX=0 NormalY=0 NormalZ=1 AngleXU=0 Radius=1.5
    g38: Circle CenterX=20 CenterY=200 CenterZ=0 NormalX=0 NormalY=0 NormalZ=1 AngleXU=0 Radius=1.5
    g39: Circle CenterX=-20 CenterY=100 CenterZ=0 NormalX=0 NormalY=0 NormalZ=1 AngleXU=0 Radius=1.5
    g40: Circle CenterX=20 CenterY=100 CenterZ=0 NormalX=0 NormalY=0 NormalZ=1 AngleXU=0 Radius=1.5
  constraints (85):
    c: Diameter(g0) = 28
    c: Coincident(g1,g0)
    c: Vertical(g1)
    c: Coincident(g2,g1)
    c: Diameter(g3) = 10
    c: Diameter(g4) = 4
    c: Coincident(g4,g1)
    c: Diameter(g5) = 4
    c: Coincident(g5,g0)
    c: Diameter(g6) = 22
    c: Tangent(g7,g9) = 1.5708
    c: Tangent(g7,g10) = -1.5708
    c: Tangent(g8,g9) = 1.5708
    c: Tangent(g8,g10) = -1.5708
    c: Equal(g7,g8)
    c: Radius(g7) = 25
    c: Coincident(g7,g3)
    c: Coincident(g8,g1)
    c: Vertical(g9)
    c: Diameter(g12) = 2.5
    c: Diameter(g13) = 2.5
    c: Diameter(g14) = 2.5
    c: Diameter(g11) = 2.5
    c: Diameter(g16) = 2.5
    c: Diameter(g17) = 2.5
    c: Diameter(g18) = 2.5
    c: Diameter(g15) = 2.5
    c: Symmetric(g10,g10,g19)
    c: Symmetric(g9,g9,g19)
    c: Distance(g20) = 30
    c: Horizontal(g20)
    c: Coincident(g20,g19)
    c: Distance(g21) = 30
    c: Horizontal(g21)
    c: Coincident(g21,g7)
    c: PointOnObject(g21,g-1)
    c: Distance(g22) = 30
    c: Horizontal(g22)
    c: Coincident(g22,g8)
    c: Coincident(g23,g20)
    c: Coincident(g23,g22)
    c: Coincident(g24,g20)
    c: Coincident(g24,g21)
    c: Symmetric(g24,g24,g25)
    c: PointOnObject(g25,g10)
    c: Horizontal(g25)
    c: Coincident(g26,g25)
    c: PointOnObject(g26,g9)
    c: Horizontal(g26)
    c: Symmetric(g23,g23,g27)
    c: PointOnObject(g27,g10)
    c: Horizontal(g27)
    c: Coincident(g28,g27)
    c: PointOnObject(g28,g9)
    c: Horizontal(g28)
    c: Distance(g29) = 5
    c: Horizontal(g29)
    c: Coincident(g29,g28)
    c: Coincident(g30,g29)
    c: PointOnObject(g30,g19)
    c: Vertical(g30)
    c: Coincident(g31,g30)
    c: PointOnObject(g31,g26)
    c: Vertical(g31)
    c: Distance(g32) = 5
    c: Horizontal(g32)
    c: Coincident(g32,g25)
    c: Coincident(g33,g32)
    c: PointOnObject(g33,g19)
    c: Vertical(g33)
    c: Coincident(g34,g33)
    c: PointOnObject(g34,g28)
    c: Vertical(g34)
    c: Diameter(g35) = 3
    c: Coincident(g35,g29)
    c: Coincident(g36,g34)
    c: Equal(g35,g36)
    c: Coincident(g37,g30)
    c: Equal(g35,g37)
    c: Coincident(g38,g33)
    c: Equal(g37,g38)
    c: Coincident(g39,g31)
    c: Equal(g37,g39)
    c: Coincident(g40,g32)
    c: Equal(g39,g40)
FEATURE [PartDesign::Pad] Pad003
  Direction = (0,0,1)
  Length = 4
  Length2 = 10
  Profile = -> Sketch003
  ReferenceAxis = -> Sketch003 [N_Axis]
  Refine = true
  Suppressed = false
  Type = 0
FEATURE [PartDesign::Body] Body005  label="arm_high_002"
  AllowCompound = false
  Group = -> [Sketch003,Pad003]
  Origin = -> Origin005
  Placement = pos=(387.832,472.58,105.3) rot=(0,0,1;1.75335rad)
  Tip = -> Pad003
COMPONENT P6 — same part as P0; its construction recipe is shown at P0.
COMPONENT P7 — same part as P0; its construction recipe is shown at P0.
COMPONENT P8 — geometry summary ("DC05_M01_DUMMY"; no construction recipe available for this part):
  bounding box: 62.1 x 50.0 x 40.2 mm
  tessellated surface: 15,904 triangles
  volume: 72104 mm^3 (58% of its bounding box)
  symmetry: mirror-symmetric across its x mid-plane
COMPONENT P9 — geometry summary ("DC05_M01_DUMMY001"; no construction recipe available for this part):
  bounding box: 62.3 x 50.0 x 40.8 mm
  tessellated surface: 15,904 triangles
  volume: 72104 mm^3 (57% of its bounding box)
  symmetry: mirror-symmetric across its x mid-plane
COMPONENT P10 — geometry summary ("DC05_M01_DUMMY002"; no construction recipe available for this part):
  bounding box: 62.1 x 50.0 x 40.2 mm
  tessellated surface: 15,904 triangles
  volume: 72104 mm^3 (58% of its bounding box)
  symmetry: mirror-symmetric across its x mid-plane
COMPONENT P11 — geometry summary ("DC05_M01_DUMMY003"; no construction recipe available for this part):
  bounding box: 62.3 x 50.0 x 40.8 mm
  tessellated surface: 15,904 triangles
  volume: 72104 mm^3 (57% of its bounding box)
  symmetry: mirror-symmetric across its x mid-plane
PROVENANCE & LICENSES
A FreeCAD (.FCStd) document from a public repository crawl; recipes are the document's own serialized feature recipes (and, for linked parts, companion documents' recipes).
License: unknown-license-file.
